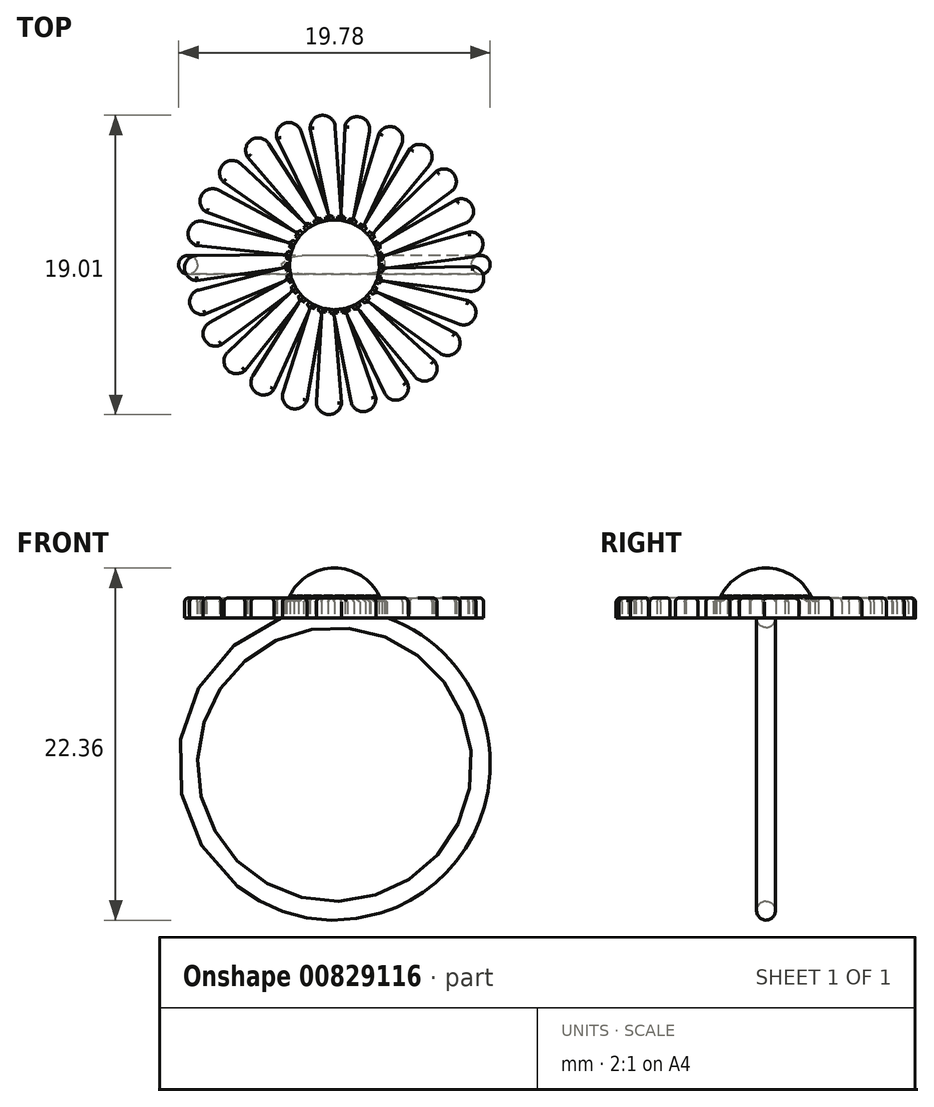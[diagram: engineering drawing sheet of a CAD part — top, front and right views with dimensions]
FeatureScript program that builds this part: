
annotation { "Feature Type Name" : "Feature", "Feature Type Description" : "" }
export const myFeature = defineFeature(function(context is Context, id is Id, definition is map)
    precondition{}
    {
        {
            var Q0;
            Q0=qCreatedBy(makeId("Top.planeOp"),FACE);
            var sketch = newSketch(context, id + "F0", { "sketchPlane" : qUnion([Q0])});
            skCircle(sketch, "E0", {"center": v(0, 0) * mm, "radius": 3.17 * mm});
            skLineSegment(sketch, "E1", {"start": v(-2.86, 1.37) * mm, "end": v(-8.13, 3.33) * mm});
            skLineSegment(sketch, "E2", {"start": v(-2.42, 2.05) * mm, "end": v(-7.36, 4.73) * mm});
            skArc(sketch, "E3", {"start": v(-7.36, 4.73) * mm, "mid": v(-8.44, 4.42) * mm, "end": v(-8.13, 3.33) * mm});
            skLineSegment(sketch, "E4.1.0", {"start": v(-2.86, 1.39) * mm, "end": v(-8.3, 2.75) * mm});
            skArc(sketch, "E4.1.1", {"start": v(-8.3, 2.75) * mm, "mid": v(-9.27, 2.18) * mm, "end": v(-8.7, 1.2) * mm});
            skLineSegment(sketch, "E4.1.2", {"start": v(-3.12, 0.61) * mm, "end": v(-8.7, 1.2) * mm});
            skLineSegment(sketch, "E4.2.0", {"start": v(-3.11, 0.63) * mm, "end": v(-8.73, 0.6) * mm});
            skArc(sketch, "E4.2.1", {"start": v(-8.73, 0.6) * mm, "mid": v(-9.52, -0.2) * mm, "end": v(-8.73, -1) * mm});
            skLineSegment(sketch, "E4.2.2", {"start": v(-3.17, -0.18) * mm, "end": v(-8.73, -1) * mm});
            skLineSegment(sketch, "E4.3.0", {"start": v(-3.17, -0.16) * mm, "end": v(-8.6, -1.6) * mm});
            skArc(sketch, "E4.3.1", {"start": v(-8.6, -1.6) * mm, "mid": v(-9.17, -2.56) * mm, "end": v(-8.21, -3.14) * mm});
            skLineSegment(sketch, "E4.3.2", {"start": v(-3.03, -0.96) * mm, "end": v(-8.21, -3.14) * mm});
            skLineSegment(sketch, "E4.4.0", {"start": v(-3.03, -0.94) * mm, "end": v(-7.94, -3.68) * mm});
            skArc(sketch, "E4.4.1", {"start": v(-7.94, -3.68) * mm, "mid": v(-8.25, -4.76) * mm, "end": v(-7.17, -5.08) * mm});
            skLineSegment(sketch, "E4.4.2", {"start": v(-2.7, -1.69) * mm, "end": v(-7.17, -5.08) * mm});
            skLineSegment(sketch, "E4.5.0", {"start": v(-2.7, -1.67) * mm, "end": v(-6.77, -5.54) * mm});
            skArc(sketch, "E4.5.1", {"start": v(-6.77, -5.54) * mm, "mid": v(-6.8, -6.66) * mm, "end": v(-5.69, -6.7) * mm});
            skLineSegment(sketch, "E4.5.2", {"start": v(-2.19, -2.3) * mm, "end": v(-5.69, -6.7) * mm});
            skLineSegment(sketch, "E4.6.0", {"start": v(-2.2, -2.29) * mm, "end": v(-5.18, -7.05) * mm});
            skArc(sketch, "E4.6.1", {"start": v(-5.18, -7.05) * mm, "mid": v(-4.94, -8.15) * mm, "end": v(-3.84, -7.9) * mm});
            skLineSegment(sketch, "E4.6.2", {"start": v(-1.55, -2.77) * mm, "end": v(-3.84, -7.9) * mm});
            skLineSegment(sketch, "E4.7.0", {"start": v(-1.56, -2.76) * mm, "end": v(-3.27, -8.12) * mm});
            skArc(sketch, "E4.7.1", {"start": v(-3.27, -8.12) * mm, "mid": v(-2.76, -9.12) * mm, "end": v(-1.75, -8.62) * mm});
            skLineSegment(sketch, "E4.7.2", {"start": v(-0.8, -3.07) * mm, "end": v(-1.75, -8.62) * mm});
            skLineSegment(sketch, "E4.8.0", {"start": v(-0.83, -3.07) * mm, "end": v(-1.15, -8.68) * mm});
            skArc(sketch, "E4.8.1", {"start": v(-1.15, -8.68) * mm, "mid": v(-0.4, -9.52) * mm, "end": v(0.45, -8.78) * mm});
            skLineSegment(sketch, "E4.8.2", {"start": v(-0.02, -3.17) * mm, "end": v(0.45, -8.78) * mm});
            skLineSegment(sketch, "E4.9.0", {"start": v(-0.04, -3.17) * mm, "end": v(1.05, -8.69) * mm});
            skArc(sketch, "E4.9.1", {"start": v(1.05, -8.69) * mm, "mid": v(1.98, -9.32) * mm, "end": v(2.62, -8.4) * mm});
            skLineSegment(sketch, "E4.9.2", {"start": v(0.77, -3.08) * mm, "end": v(2.62, -8.4) * mm});
            skLineSegment(sketch, "E4.10.0", {"start": v(0.75, -3.08) * mm, "end": v(3.18, -8.15) * mm});
            skArc(sketch, "E4.10.1", {"start": v(3.18, -8.15) * mm, "mid": v(4.23, -8.53) * mm, "end": v(4.62, -7.48) * mm});
            skLineSegment(sketch, "E4.10.2", {"start": v(1.51, -2.8) * mm, "end": v(4.62, -7.48) * mm});
            skLineSegment(sketch, "E4.11.0", {"start": v(1.5, -2.8) * mm, "end": v(5.1, -7.1) * mm});
            skArc(sketch, "E4.11.1", {"start": v(5.1, -7.1) * mm, "mid": v(6.22, -7.21) * mm, "end": v(6.34, -6.1) * mm});
            skLineSegment(sketch, "E4.11.2", {"start": v(2.16, -2.33) * mm, "end": v(6.34, -6.1) * mm});
            skLineSegment(sketch, "E4.12.0", {"start": v(2.14, -2.34) * mm, "end": v(6.71, -5.62) * mm});
            skArc(sketch, "E4.12.1", {"start": v(6.71, -5.62) * mm, "mid": v(7.82, -5.44) * mm, "end": v(7.65, -4.33) * mm});
            skLineSegment(sketch, "E4.12.2", {"start": v(2.67, -1.72) * mm, "end": v(7.65, -4.33) * mm});
            skLineSegment(sketch, "E4.13.0", {"start": v(2.66, -1.73) * mm, "end": v(7.9, -3.77) * mm});
            skArc(sketch, "E4.13.1", {"start": v(7.9, -3.77) * mm, "mid": v(8.93, -3.32) * mm, "end": v(8.49, -2.29) * mm});
            skLineSegment(sketch, "E4.13.2", {"start": v(3.01, -1) * mm, "end": v(8.49, -2.29) * mm});
            skLineSegment(sketch, "E4.14.0", {"start": v(3, -1.02) * mm, "end": v(8.59, -1.69) * mm});
            skArc(sketch, "E4.14.1", {"start": v(8.59, -1.69) * mm, "mid": v(9.47, -1) * mm, "end": v(8.8, -0.1) * mm});
            skLineSegment(sketch, "E4.14.2", {"start": v(3.17, -0.22) * mm, "end": v(8.8, -0.1) * mm});
            skLineSegment(sketch, "E4.15.0", {"start": v(3.17, -0.24) * mm, "end": v(8.74, 0.5) * mm});
            skArc(sketch, "E4.15.1", {"start": v(8.74, 0.5) * mm, "mid": v(9.42, 1.39) * mm, "end": v(8.54, 2.08) * mm});
            skLineSegment(sketch, "E4.15.2", {"start": v(3.12, 0.58) * mm, "end": v(8.54, 2.08) * mm});
            skLineSegment(sketch, "E4.16.0", {"start": v(3.13, 0.56) * mm, "end": v(8.34, 2.66) * mm});
            skArc(sketch, "E4.16.1", {"start": v(8.34, 2.66) * mm, "mid": v(8.78, 3.69) * mm, "end": v(7.75, 4.14) * mm});
            skLineSegment(sketch, "E4.16.2", {"start": v(2.88, 1.33) * mm, "end": v(7.75, 4.14) * mm});
            skLineSegment(sketch, "E4.17.0", {"start": v(2.89, 1.32) * mm, "end": v(7.41, 4.65) * mm});
            skArc(sketch, "E4.17.1", {"start": v(7.41, 4.65) * mm, "mid": v(7.59, 5.76) * mm, "end": v(6.48, 5.94) * mm});
            skLineSegment(sketch, "E4.17.2", {"start": v(2.46, 2) * mm, "end": v(6.48, 5.94) * mm});
            skLineSegment(sketch, "E4.18.0", {"start": v(2.47, 2) * mm, "end": v(6.03, 6.35) * mm});
            skArc(sketch, "E4.18.1", {"start": v(6.03, 6.35) * mm, "mid": v(5.92, 7.46) * mm, "end": v(4.8, 7.37) * mm});
            skLineSegment(sketch, "E4.18.2", {"start": v(1.88, 2.56) * mm, "end": v(4.8, 7.37) * mm});
            skLineSegment(sketch, "E4.19.0", {"start": v(1.9, 2.55) * mm, "end": v(4.26, 7.64) * mm});
            skArc(sketch, "E4.19.1", {"start": v(4.26, 7.64) * mm, "mid": v(3.88, 8.7) * mm, "end": v(2.82, 8.33) * mm});
            skLineSegment(sketch, "E4.19.2", {"start": v(1.19, 2.95) * mm, "end": v(2.82, 8.33) * mm});
            skLineSegment(sketch, "E4.20.0", {"start": v(1.2, 2.94) * mm, "end": v(2.22, 8.46) * mm});
            skArc(sketch, "E4.20.1", {"start": v(2.22, 8.46) * mm, "mid": v(1.6, 9.4) * mm, "end": v(0.66, 8.77) * mm});
            skLineSegment(sketch, "E4.20.2", {"start": v(0.42, 3.15) * mm, "end": v(0.66, 8.77) * mm});
            skLineSegment(sketch, "E4.21.0", {"start": v(0.44, 3.14) * mm, "end": v(0.05, 8.75) * mm});
            skArc(sketch, "E4.21.1", {"start": v(0.05, 8.75) * mm, "mid": v(-0.8, 9.5) * mm, "end": v(-1.54, 8.65) * mm});
            skLineSegment(sketch, "E4.21.2", {"start": v(-0.38, 3.15) * mm, "end": v(-1.54, 8.65) * mm});
            skLineSegment(sketch, "E4.22.0", {"start": v(-0.36, 3.15) * mm, "end": v(-2.13, 8.49) * mm});
            skArc(sketch, "E4.22.1", {"start": v(-2.13, 8.49) * mm, "mid": v(-3.13, 9) * mm, "end": v(-3.65, 8) * mm});
            skLineSegment(sketch, "E4.22.2", {"start": v(-1.15, 2.96) * mm, "end": v(-3.65, 8) * mm});
            skLineSegment(sketch, "E4.23.0", {"start": v(-1.13, 2.97) * mm, "end": v(-4.17, 7.7) * mm});
            skArc(sketch, "E4.23.1", {"start": v(-4.17, 7.7) * mm, "mid": v(-5.27, 7.93) * mm, "end": v(-5.52, 6.84) * mm});
            skLineSegment(sketch, "E4.23.2", {"start": v(-1.85, 2.58) * mm, "end": v(-5.52, 6.84) * mm});
            skLineSegment(sketch, "E4.24.0", {"start": v(-1.83, 2.6) * mm, "end": v(-5.95, 6.41) * mm});
            skArc(sketch, "E4.24.1", {"start": v(-5.95, 6.41) * mm, "mid": v(-7.08, 6.38) * mm, "end": v(-7.05, 5.25) * mm});
            skLineSegment(sketch, "E4.24.2", {"start": v(-2.43, 2.04) * mm, "end": v(-7.05, 5.25) * mm});
            skLineSegment(sketch, "E5", {"start": v(0, 0) * mm, "end": v(0, 3.17) * mm});
            skLineSegment(sketch, "E6", {"start": v(0, 0) * mm, "end": v(0, -3.17) * mm});
            skLineSegment(sketch, "E7", {"start": v(0, 3.17) * mm, "end": v(0, -3.17) * mm, "construction": true});
            skSolve(sketch);
        }
        {
            var Q0;
            Q0 = qSketchRegion(id + "F0", true);
            var Q1;
            {var subQ18=sQuery(id+"F0.wireOp",EDGE,"E5");Q1=makeQuery(id+"F0.imprint","IMPRINT",FACE,{"disambiguationData":[TD([[makeQuery(id+"F0.imprint","IMPRINT",EDGE,{"derivedFrom":subQ18}),1.0]])]});}
            var Q2;
            {var subQ4=sQuery(id+"F0.wireOp",EDGE,"E5");Q2=makeQuery(id+"F0.imprint","IMPRINT",FACE,{"disambiguationData":[TD([[makeQuery(id+"F0.imprint","IMPRINT",EDGE,{"derivedFrom":subQ4}),-1.0]])]});}
            extrude(context, id + "F1", {"entities" : qUnion([Q0, Q1, Q2]), "depth" : 1.27 * mm, "offsetDistance" : 25.4 * mm});
        }
        {
            var Q0;
            {var subQ18=sQuery(id+"F0.wireOp",EDGE,"E5");Q0=makeQuery(id+"F0.imprint","IMPRINT",FACE,{"disambiguationData":[TD([[makeQuery(id+"F0.imprint","IMPRINT",EDGE,{"derivedFrom":subQ18}),1.0]])]});}
            var Q1;
            Q1=sQuery(id+"F0.wireOp",EDGE,"E6");
            revolve(context, id + "F2", {"operationType" : NewBodyOperationType.ADD, "surfaceOperationType" : NewSurfaceOperationType.NEW, "entities" : qUnion([Q0]), "axis" : qUnion([Q1]), "revolveType" : RevolveType.ONE_DIRECTION, "oppositeDirection" : true, "angle" : 180 * degree});
        }
        {
            var Q0;
            Q0=makeQuery(id+"F1.opExtrude","CAP_EDGE",EDGE,{"disambiguationData":[OSD([sQuery(id+"F0.wireOp",EDGE,"E3")])],"isStart":false});
            var Q1;
            Q1=makeQuery(id+"F1.opExtrude","CAP_EDGE",EDGE,{"disambiguationData":[OSD([sQuery(id+"F0.wireOp",EDGE,"E1")])],"isStart":false});
            var Q2;
            Q2=makeQuery(id+"F1.opExtrude","CAP_EDGE",EDGE,{"disambiguationData":[OSD([sQuery(id+"F0.wireOp",EDGE,"E2")])],"isStart":false});
            var Q3;
            Q3=makeQuery(id+"F1.opExtrude","CAP_EDGE",EDGE,{"disambiguationData":[OSD([sQuery(id+"F0.wireOp",EDGE,"E4.24.1")])],"isStart":false});
            var Q4;
            Q4=makeQuery(id+"F1.opExtrude","CAP_EDGE",EDGE,{"disambiguationData":[OSD([sQuery(id+"F0.wireOp",EDGE,"E4.24.2")])],"isStart":false});
            var Q5;
            Q5=makeQuery(id+"F1.opExtrude","CAP_EDGE",EDGE,{"disambiguationData":[OSD([sQuery(id+"F0.wireOp",EDGE,"E4.24.0")])],"isStart":false});
            var Q6;
            Q6=makeQuery(id+"F1.opExtrude","CAP_EDGE",EDGE,{"disambiguationData":[OSD([sQuery(id+"F0.wireOp",EDGE,"E4.23.2")])],"isStart":false});
            var Q7;
            Q7=makeQuery(id+"F1.opExtrude","CAP_EDGE",EDGE,{"disambiguationData":[OSD([sQuery(id+"F0.wireOp",EDGE,"E4.23.1")])],"isStart":false});
            var Q8;
            Q8=makeQuery(id+"F1.opExtrude","CAP_EDGE",EDGE,{"disambiguationData":[OSD([sQuery(id+"F0.wireOp",EDGE,"E4.23.0")])],"isStart":false});
            var Q9;
            Q9=makeQuery(id+"F1.opExtrude","CAP_EDGE",EDGE,{"disambiguationData":[OSD([sQuery(id+"F0.wireOp",EDGE,"E4.22.2")])],"isStart":false});
            var Q10;
            Q10=makeQuery(id+"F1.opExtrude","CAP_EDGE",EDGE,{"disambiguationData":[OSD([sQuery(id+"F0.wireOp",EDGE,"E4.22.1")])],"isStart":false});
            var Q11;
            Q11=makeQuery(id+"F1.opExtrude","CAP_EDGE",EDGE,{"disambiguationData":[OSD([sQuery(id+"F0.wireOp",EDGE,"E4.22.0")])],"isStart":false});
            var Q12;
            Q12=makeQuery(id+"F1.opExtrude","CAP_EDGE",EDGE,{"disambiguationData":[OSD([sQuery(id+"F0.wireOp",EDGE,"E4.21.1")])],"isStart":false});
            var Q13;
            Q13=makeQuery(id+"F1.opExtrude","CAP_EDGE",EDGE,{"disambiguationData":[OSD([sQuery(id+"F0.wireOp",EDGE,"E4.21.2")])],"isStart":false});
            var Q14;
            Q14=makeQuery(id+"F1.opExtrude","CAP_EDGE",EDGE,{"disambiguationData":[OSD([sQuery(id+"F0.wireOp",EDGE,"E4.21.0")])],"isStart":false});
            var Q15;
            Q15=makeQuery(id+"F1.opExtrude","CAP_EDGE",EDGE,{"disambiguationData":[OSD([sQuery(id+"F0.wireOp",EDGE,"E4.20.2")])],"isStart":false});
            var Q16;
            Q16=makeQuery(id+"F1.opExtrude","CAP_EDGE",EDGE,{"disambiguationData":[OSD([sQuery(id+"F0.wireOp",EDGE,"E4.20.1")])],"isStart":false});
            var Q17;
            Q17=makeQuery(id+"F1.opExtrude","CAP_EDGE",EDGE,{"disambiguationData":[OSD([sQuery(id+"F0.wireOp",EDGE,"E4.19.2")])],"isStart":false});
            var Q18;
            Q18=makeQuery(id+"F1.opExtrude","CAP_EDGE",EDGE,{"disambiguationData":[OSD([sQuery(id+"F0.wireOp",EDGE,"E4.19.1")])],"isStart":false});
            var Q19;
            Q19=makeQuery(id+"F1.opExtrude","CAP_EDGE",EDGE,{"disambiguationData":[OSD([sQuery(id+"F0.wireOp",EDGE,"E4.19.0")])],"isStart":false});
            var Q20;
            Q20=makeQuery(id+"F1.opExtrude","CAP_EDGE",EDGE,{"disambiguationData":[OSD([sQuery(id+"F0.wireOp",EDGE,"E4.1.1")])],"isStart":false});
            var Q21;
            Q21=makeQuery(id+"F1.opExtrude","CAP_EDGE",EDGE,{"disambiguationData":[OSD([sQuery(id+"F0.wireOp",EDGE,"E4.1.2")])],"isStart":false});
            var Q22;
            Q22=makeQuery(id+"F1.opExtrude","CAP_EDGE",EDGE,{"disambiguationData":[OSD([sQuery(id+"F0.wireOp",EDGE,"E4.1.0")])],"isStart":false});
            var Q23;
            Q23=makeQuery(id+"F1.opExtrude","CAP_EDGE",EDGE,{"disambiguationData":[OSD([sQuery(id+"F0.wireOp",EDGE,"E4.2.1")])],"isStart":false});
            var Q24;
            Q24=makeQuery(id+"F1.opExtrude","CAP_EDGE",EDGE,{"disambiguationData":[OSD([sQuery(id+"F0.wireOp",EDGE,"E4.2.0")])],"isStart":false});
            var Q25;
            Q25=makeQuery(id+"F1.opExtrude","CAP_EDGE",EDGE,{"disambiguationData":[OSD([sQuery(id+"F0.wireOp",EDGE,"E4.18.2")])],"isStart":false});
            var Q26;
            Q26=makeQuery(id+"F1.opExtrude","CAP_EDGE",EDGE,{"disambiguationData":[OSD([sQuery(id+"F0.wireOp",EDGE,"E4.18.0")])],"isStart":false});
            var Q27;
            Q27=makeQuery(id+"F1.opExtrude","CAP_EDGE",EDGE,{"disambiguationData":[OSD([sQuery(id+"F0.wireOp",EDGE,"E4.18.1")])],"isStart":false});
            var Q28;
            Q28=makeQuery(id+"F1.opExtrude","CAP_EDGE",EDGE,{"disambiguationData":[OSD([sQuery(id+"F0.wireOp",EDGE,"E4.17.1")])],"isStart":false});
            var Q29;
            Q29=makeQuery(id+"F1.opExtrude","CAP_EDGE",EDGE,{"disambiguationData":[OSD([sQuery(id+"F0.wireOp",EDGE,"E4.17.2")])],"isStart":false});
            var Q30;
            Q30=makeQuery(id+"F1.opExtrude","CAP_EDGE",EDGE,{"disambiguationData":[OSD([sQuery(id+"F0.wireOp",EDGE,"E4.17.0")])],"isStart":false});
            var Q31;
            Q31=makeQuery(id+"F1.opExtrude","CAP_EDGE",EDGE,{"disambiguationData":[OSD([sQuery(id+"F0.wireOp",EDGE,"E4.16.2")])],"isStart":false});
            var Q32;
            Q32=makeQuery(id+"F1.opExtrude","CAP_EDGE",EDGE,{"disambiguationData":[OSD([sQuery(id+"F0.wireOp",EDGE,"E4.16.1")])],"isStart":false});
            var Q33;
            Q33=makeQuery(id+"F1.opExtrude","CAP_EDGE",EDGE,{"disambiguationData":[OSD([sQuery(id+"F0.wireOp",EDGE,"E4.16.0")])],"isStart":false});
            var Q34;
            Q34=makeQuery(id+"F1.opExtrude","CAP_EDGE",EDGE,{"disambiguationData":[OSD([sQuery(id+"F0.wireOp",EDGE,"E4.15.2")])],"isStart":false});
            var Q35;
            Q35=makeQuery(id+"F1.opExtrude","CAP_EDGE",EDGE,{"disambiguationData":[OSD([sQuery(id+"F0.wireOp",EDGE,"E4.15.1")])],"isStart":false});
            var Q36;
            Q36=makeQuery(id+"F1.opExtrude","CAP_EDGE",EDGE,{"disambiguationData":[OSD([sQuery(id+"F0.wireOp",EDGE,"E4.15.0")])],"isStart":false});
            var Q37;
            Q37=makeQuery(id+"F1.opExtrude","CAP_EDGE",EDGE,{"disambiguationData":[OSD([sQuery(id+"F0.wireOp",EDGE,"E4.14.2")])],"isStart":false});
            var Q38;
            Q38=makeQuery(id+"F1.opExtrude","CAP_EDGE",EDGE,{"disambiguationData":[OSD([sQuery(id+"F0.wireOp",EDGE,"E4.14.1")])],"isStart":false});
            var Q39;
            Q39=makeQuery(id+"F1.opExtrude","CAP_EDGE",EDGE,{"disambiguationData":[OSD([sQuery(id+"F0.wireOp",EDGE,"E4.14.0")])],"isStart":false});
            var Q40;
            Q40=makeQuery(id+"F1.opExtrude","CAP_EDGE",EDGE,{"disambiguationData":[OSD([sQuery(id+"F0.wireOp",EDGE,"E4.13.2")])],"isStart":false});
            var Q41;
            Q41=makeQuery(id+"F1.opExtrude","CAP_EDGE",EDGE,{"disambiguationData":[OSD([sQuery(id+"F0.wireOp",EDGE,"E4.13.1")])],"isStart":false});
            var Q42;
            Q42=makeQuery(id+"F1.opExtrude","CAP_EDGE",EDGE,{"disambiguationData":[OSD([sQuery(id+"F0.wireOp",EDGE,"E4.13.0")])],"isStart":false});
            var Q43;
            Q43=makeQuery(id+"F1.opExtrude","CAP_EDGE",EDGE,{"disambiguationData":[OSD([sQuery(id+"F0.wireOp",EDGE,"E4.12.2")])],"isStart":false});
            var Q44;
            Q44=makeQuery(id+"F1.opExtrude","CAP_EDGE",EDGE,{"disambiguationData":[OSD([sQuery(id+"F0.wireOp",EDGE,"E4.12.1")])],"isStart":false});
            var Q45;
            Q45=makeQuery(id+"F1.opExtrude","CAP_EDGE",EDGE,{"disambiguationData":[OSD([sQuery(id+"F0.wireOp",EDGE,"E4.12.0")])],"isStart":false});
            var Q46;
            Q46=makeQuery(id+"F1.opExtrude","CAP_EDGE",EDGE,{"disambiguationData":[OSD([sQuery(id+"F0.wireOp",EDGE,"E4.11.2")])],"isStart":false});
            var Q47;
            Q47=makeQuery(id+"F1.opExtrude","CAP_EDGE",EDGE,{"disambiguationData":[OSD([sQuery(id+"F0.wireOp",EDGE,"E4.11.1")])],"isStart":false});
            var Q48;
            Q48=makeQuery(id+"F1.opExtrude","CAP_EDGE",EDGE,{"disambiguationData":[OSD([sQuery(id+"F0.wireOp",EDGE,"E4.11.0")])],"isStart":false});
            var Q49;
            Q49=makeQuery(id+"F1.opExtrude","CAP_EDGE",EDGE,{"disambiguationData":[OSD([sQuery(id+"F0.wireOp",EDGE,"E4.10.2")])],"isStart":false});
            var Q50;
            Q50=makeQuery(id+"F1.opExtrude","CAP_EDGE",EDGE,{"disambiguationData":[OSD([sQuery(id+"F0.wireOp",EDGE,"E4.10.1")])],"isStart":false});
            var Q51;
            Q51=makeQuery(id+"F1.opExtrude","CAP_EDGE",EDGE,{"disambiguationData":[OSD([sQuery(id+"F0.wireOp",EDGE,"E4.10.0")])],"isStart":false});
            var Q52;
            Q52=makeQuery(id+"F1.opExtrude","CAP_EDGE",EDGE,{"disambiguationData":[OSD([sQuery(id+"F0.wireOp",EDGE,"E4.2.2")])],"isStart":false});
            var Q53;
            Q53=makeQuery(id+"F1.opExtrude","CAP_EDGE",EDGE,{"disambiguationData":[OSD([sQuery(id+"F0.wireOp",EDGE,"E4.3.0")])],"isStart":false});
            var Q54;
            Q54=makeQuery(id+"F1.opExtrude","CAP_EDGE",EDGE,{"disambiguationData":[OSD([sQuery(id+"F0.wireOp",EDGE,"E4.3.1")])],"isStart":false});
            var Q55;
            Q55=makeQuery(id+"F1.opExtrude","CAP_EDGE",EDGE,{"disambiguationData":[OSD([sQuery(id+"F0.wireOp",EDGE,"E4.3.2")])],"isStart":false});
            var Q56;
            Q56=makeQuery(id+"F1.opExtrude","CAP_EDGE",EDGE,{"disambiguationData":[OSD([sQuery(id+"F0.wireOp",EDGE,"E4.4.0")])],"isStart":false});
            var Q57;
            Q57=makeQuery(id+"F1.opExtrude","CAP_EDGE",EDGE,{"disambiguationData":[OSD([sQuery(id+"F0.wireOp",EDGE,"E4.4.1")])],"isStart":false});
            var Q58;
            Q58=makeQuery(id+"F1.opExtrude","CAP_EDGE",EDGE,{"disambiguationData":[OSD([sQuery(id+"F0.wireOp",EDGE,"E4.4.2")])],"isStart":false});
            var Q59;
            Q59=makeQuery(id+"F1.opExtrude","CAP_EDGE",EDGE,{"disambiguationData":[OSD([sQuery(id+"F0.wireOp",EDGE,"E4.5.0")])],"isStart":false});
            var Q60;
            Q60=makeQuery(id+"F1.opExtrude","CAP_EDGE",EDGE,{"disambiguationData":[OSD([sQuery(id+"F0.wireOp",EDGE,"E4.5.1")])],"isStart":false});
            var Q61;
            Q61=makeQuery(id+"F1.opExtrude","CAP_EDGE",EDGE,{"disambiguationData":[OSD([sQuery(id+"F0.wireOp",EDGE,"E4.5.2")])],"isStart":false});
            var Q62;
            Q62=makeQuery(id+"F1.opExtrude","CAP_EDGE",EDGE,{"disambiguationData":[OSD([sQuery(id+"F0.wireOp",EDGE,"E4.6.0")])],"isStart":false});
            var Q63;
            Q63=makeQuery(id+"F1.opExtrude","CAP_EDGE",EDGE,{"disambiguationData":[OSD([sQuery(id+"F0.wireOp",EDGE,"E4.6.1")])],"isStart":false});
            var Q64;
            Q64=makeQuery(id+"F1.opExtrude","CAP_EDGE",EDGE,{"disambiguationData":[OSD([sQuery(id+"F0.wireOp",EDGE,"E4.6.2")])],"isStart":false});
            var Q65;
            Q65=makeQuery(id+"F1.opExtrude","CAP_EDGE",EDGE,{"disambiguationData":[OSD([sQuery(id+"F0.wireOp",EDGE,"E4.7.0")])],"isStart":false});
            var Q66;
            Q66=makeQuery(id+"F1.opExtrude","CAP_EDGE",EDGE,{"disambiguationData":[OSD([sQuery(id+"F0.wireOp",EDGE,"E4.7.1")])],"isStart":false});
            var Q67;
            Q67=makeQuery(id+"F1.opExtrude","CAP_EDGE",EDGE,{"disambiguationData":[OSD([sQuery(id+"F0.wireOp",EDGE,"E4.7.2")])],"isStart":false});
            var Q68;
            Q68=makeQuery(id+"F1.opExtrude","CAP_EDGE",EDGE,{"disambiguationData":[OSD([sQuery(id+"F0.wireOp",EDGE,"E4.8.0")])],"isStart":false});
            var Q69;
            Q69=makeQuery(id+"F1.opExtrude","CAP_EDGE",EDGE,{"disambiguationData":[OSD([sQuery(id+"F0.wireOp",EDGE,"E4.8.1")])],"isStart":false});
            var Q70;
            Q70=makeQuery(id+"F1.opExtrude","CAP_EDGE",EDGE,{"disambiguationData":[OSD([sQuery(id+"F0.wireOp",EDGE,"E4.8.2")])],"isStart":false});
            var Q71;
            Q71=makeQuery(id+"F1.opExtrude","CAP_EDGE",EDGE,{"disambiguationData":[OSD([sQuery(id+"F0.wireOp",EDGE,"E4.9.0")])],"isStart":false});
            var Q72;
            Q72=makeQuery(id+"F1.opExtrude","CAP_EDGE",EDGE,{"disambiguationData":[OSD([sQuery(id+"F0.wireOp",EDGE,"E4.9.1")])],"isStart":false});
            var Q73;
            Q73=makeQuery(id+"F1.opExtrude","CAP_EDGE",EDGE,{"disambiguationData":[OSD([sQuery(id+"F0.wireOp",EDGE,"E4.9.2")])],"isStart":false});
            var Q74;
            Q74=makeQuery(id+"F1.opExtrude","CAP_EDGE",EDGE,{"disambiguationData":[OSD([sQuery(id+"F0.wireOp",EDGE,"E4.20.0")])],"isStart":false});
            fillet(context, id + "F3", {"entities" : qUnion([Q0, Q1, Q2, Q3, Q4, Q5, Q6, Q7, Q8, Q9, Q10, Q11, Q12, Q13, Q14, Q15, Q16, Q17, Q18, Q19, Q20, Q21, Q22, Q23, Q24, Q25, Q26, Q27, Q28, Q29, Q30, Q31, Q32, Q33, Q34, Q35, Q36, Q37, Q38, Q39, Q40, Q41, Q42, Q43, Q44, Q45, Q46, Q47, Q48, Q49, Q50, Q51, Q52, Q53, Q54, Q55, Q56, Q57, Q58, Q59, Q60, Q61, Q62, Q63, Q64, Q65, Q66, Q67, Q68, Q69, Q70, Q71, Q72, Q73, Q74]), "radius" : 0.25 * mm, "tangentPropagation" : true, "allowEdgeOverflow" : false});
        }
        {
            var Q0;
            Q0=qCreatedBy(makeId("Right.planeOp"),FACE);
            var sketch = newSketch(context, id + "F4", { "sketchPlane" : qUnion([Q0])});
            skCircle(sketch, "E8", {"center": v(0, 0) * mm, "radius": 0.6 * mm});
            skLineSegment(sketch, "E9", {"start": v(0, 0) * mm, "end": v(0, -18.6) * mm, "construction": true});
            skCircle(sketch, "E10", {"center": v(0, -18.6) * mm, "radius": 0.6 * mm});
            skPoint(sketch, "E11", {"position": v(0, -9.3) * mm});
            skLineSegment(sketch, "E12", {"start": v(-8.96, -9.3) * mm, "end": v(8.87, -9.3) * mm, "construction": true});
            skSolve(sketch);
        }
        {
            var Q0;
            Q0=makeQuery(id+"F4.imprint","IMPRINT",FACE,{"disambiguationData":[TD([[makeQuery(id+"F4.imprint","IMPRINT",EDGE,{"derivedFrom":sQuery(id+"F4.wireOp",EDGE,"E10")}),1.0]])]});
            var Q1;
            Q1=sQuery(id+"F4.wireOp",EDGE,"E12");
            revolve(context, id + "F5", {"operationType" : NewBodyOperationType.ADD, "surfaceOperationType" : NewSurfaceOperationType.NEW, "entities" : qUnion([Q0]), "axis" : qUnion([Q1]), "revolveType" : RevolveType.FULL});
        }
        {
            var Q0;
            Q0=makeQuery(id+"F2.boolean.opBoolean","INTERSECT",EDGE,{"derivedFrom":[makeQuery(id+"F1.opExtrude","CAP_FACE",FACE,{"disambiguationData":[OSD([sQuery(id+"F0.wireOp",EDGE,"E1"),sQuery(id+"F0.wireOp",EDGE,"E2"),sQuery(id+"F0.wireOp",EDGE,"E3"),sQuery(id+"F0.wireOp",EDGE,"E4.1.0"),sQuery(id+"F0.wireOp",EDGE,"E4.1.1"),sQuery(id+"F0.wireOp",EDGE,"E4.1.2"),sQuery(id+"F0.wireOp",EDGE,"E4.2.0"),sQuery(id+"F0.wireOp",EDGE,"E4.2.1"),sQuery(id+"F0.wireOp",EDGE,"E4.2.2"),sQuery(id+"F0.wireOp",EDGE,"E4.3.0"),sQuery(id+"F0.wireOp",EDGE,"E4.3.1"),sQuery(id+"F0.wireOp",EDGE,"E4.3.2"),sQuery(id+"F0.wireOp",EDGE,"E4.4.0"),sQuery(id+"F0.wireOp",EDGE,"E4.4.1"),sQuery(id+"F0.wireOp",EDGE,"E4.4.2"),sQuery(id+"F0.wireOp",EDGE,"E4.5.0"),sQuery(id+"F0.wireOp",EDGE,"E4.5.1"),sQuery(id+"F0.wireOp",EDGE,"E4.5.2"),sQuery(id+"F0.wireOp",EDGE,"E4.6.0"),sQuery(id+"F0.wireOp",EDGE,"E4.6.1"),sQuery(id+"F0.wireOp",EDGE,"E4.6.2"),sQuery(id+"F0.wireOp",EDGE,"E4.7.0"),sQuery(id+"F0.wireOp",EDGE,"E4.7.1"),sQuery(id+"F0.wireOp",EDGE,"E4.7.2"),sQuery(id+"F0.wireOp",EDGE,"E4.8.0"),sQuery(id+"F0.wireOp",EDGE,"E4.8.1"),sQuery(id+"F0.wireOp",EDGE,"E4.8.2"),sQuery(id+"F0.wireOp",EDGE,"E4.9.0"),sQuery(id+"F0.wireOp",EDGE,"E4.9.1"),sQuery(id+"F0.wireOp",EDGE,"E4.9.2"),sQuery(id+"F0.wireOp",EDGE,"E4.10.0"),sQuery(id+"F0.wireOp",EDGE,"E4.10.1"),sQuery(id+"F0.wireOp",EDGE,"E4.10.2"),sQuery(id+"F0.wireOp",EDGE,"E4.11.0"),sQuery(id+"F0.wireOp",EDGE,"E4.11.1"),sQuery(id+"F0.wireOp",EDGE,"E4.11.2"),sQuery(id+"F0.wireOp",EDGE,"E4.12.0"),sQuery(id+"F0.wireOp",EDGE,"E4.12.1"),sQuery(id+"F0.wireOp",EDGE,"E4.12.2"),sQuery(id+"F0.wireOp",EDGE,"E4.13.0"),sQuery(id+"F0.wireOp",EDGE,"E4.13.1"),sQuery(id+"F0.wireOp",EDGE,"E4.13.2"),sQuery(id+"F0.wireOp",EDGE,"E4.14.0"),sQuery(id+"F0.wireOp",EDGE,"E4.14.1"),sQuery(id+"F0.wireOp",EDGE,"E4.14.2"),sQuery(id+"F0.wireOp",EDGE,"E4.15.0"),sQuery(id+"F0.wireOp",EDGE,"E4.15.1"),sQuery(id+"F0.wireOp",EDGE,"E4.15.2"),sQuery(id+"F0.wireOp",EDGE,"E4.16.0"),sQuery(id+"F0.wireOp",EDGE,"E4.16.1"),sQuery(id+"F0.wireOp",EDGE,"E4.16.2"),sQuery(id+"F0.wireOp",EDGE,"E4.17.0"),sQuery(id+"F0.wireOp",EDGE,"E4.17.1"),sQuery(id+"F0.wireOp",EDGE,"E4.17.2"),sQuery(id+"F0.wireOp",EDGE,"E4.18.0"),sQuery(id+"F0.wireOp",EDGE,"E4.18.1"),sQuery(id+"F0.wireOp",EDGE,"E4.18.2"),sQuery(id+"F0.wireOp",EDGE,"E4.19.0"),sQuery(id+"F0.wireOp",EDGE,"E4.19.1"),sQuery(id+"F0.wireOp",EDGE,"E4.19.2"),sQuery(id+"F0.wireOp",EDGE,"E4.20.0"),sQuery(id+"F0.wireOp",EDGE,"E4.20.1"),sQuery(id+"F0.wireOp",EDGE,"E4.20.2"),sQuery(id+"F0.wireOp",EDGE,"E4.21.0"),sQuery(id+"F0.wireOp",EDGE,"E4.21.1"),sQuery(id+"F0.wireOp",EDGE,"E4.21.2"),sQuery(id+"F0.wireOp",EDGE,"E4.22.0"),sQuery(id+"F0.wireOp",EDGE,"E4.22.1"),sQuery(id+"F0.wireOp",EDGE,"E4.22.2"),sQuery(id+"F0.wireOp",EDGE,"E4.23.0"),sQuery(id+"F0.wireOp",EDGE,"E4.23.1"),sQuery(id+"F0.wireOp",EDGE,"E4.23.2"),sQuery(id+"F0.wireOp",EDGE,"E4.24.0"),sQuery(id+"F0.wireOp",EDGE,"E4.24.1"),sQuery(id+"F0.wireOp",EDGE,"E4.24.2")])],"isStart":false}),makeQuery(id+"F2.opRevolve","SWEPT_FACE",FACE,{"disambiguationData":[OSD([sQuery(id+"F0.wireOp",EDGE,"E0")])]})]});
            var Q1;
            Q1=makeQuery(id+"F3.opFillet","BLEND_EDGE",EDGE,{"blendedFrom":[makeQuery(id+"F1.opExtrude","CAP_EDGE",EDGE,{"disambiguationData":[OSD([sQuery(id+"F0.wireOp",EDGE,"E4.24.0")])],"isStart":false}),makeQuery(id+"F2.opRevolve","SWEPT_FACE",FACE,{"disambiguationData":[OSD([sQuery(id+"F0.wireOp",EDGE,"E0")])]})],"blendedInto":[makeQuery(id+"F2.opRevolve","SWEPT_FACE",FACE,{"disambiguationData":[OSD([sQuery(id+"F0.wireOp",EDGE,"E0")])]})]});
            var Q2;
            Q2=makeQuery(id+"F3.opFillet","BLEND_EDGE",EDGE,{"blendedFrom":[makeQuery(id+"F1.opExtrude","CAP_EDGE",EDGE,{"disambiguationData":[OSD([sQuery(id+"F0.wireOp",EDGE,"E4.24.2")])],"isStart":false}),makeQuery(id+"F2.opRevolve","SWEPT_FACE",FACE,{"disambiguationData":[OSD([sQuery(id+"F0.wireOp",EDGE,"E0")])]})],"blendedInto":[makeQuery(id+"F2.opRevolve","SWEPT_FACE",FACE,{"disambiguationData":[OSD([sQuery(id+"F0.wireOp",EDGE,"E0")])]})]});
            var Q3;
            Q3=makeQuery(id+"F3.opFillet","BLEND_EDGE",EDGE,{"blendedFrom":[makeQuery(id+"F1.opExtrude","CAP_EDGE",EDGE,{"disambiguationData":[OSD([sQuery(id+"F0.wireOp",EDGE,"E2")])],"isStart":false}),makeQuery(id+"F2.opRevolve","SWEPT_FACE",FACE,{"disambiguationData":[OSD([sQuery(id+"F0.wireOp",EDGE,"E0")])]})],"blendedInto":[makeQuery(id+"F2.opRevolve","SWEPT_FACE",FACE,{"disambiguationData":[OSD([sQuery(id+"F0.wireOp",EDGE,"E0")])]})]});
            var Q4;
            Q4=makeQuery(id+"F3.opFillet","BLEND_EDGE",EDGE,{"blendedFrom":[makeQuery(id+"F1.opExtrude","CAP_EDGE",EDGE,{"disambiguationData":[OSD([sQuery(id+"F0.wireOp",EDGE,"E1")])],"isStart":false}),makeQuery(id+"F2.opRevolve","SWEPT_FACE",FACE,{"disambiguationData":[OSD([sQuery(id+"F0.wireOp",EDGE,"E0")])]})],"blendedInto":[makeQuery(id+"F2.opRevolve","SWEPT_FACE",FACE,{"disambiguationData":[OSD([sQuery(id+"F0.wireOp",EDGE,"E0")])]})]});
            var Q5;
            Q5=makeQuery(id+"F3.opFillet","BLEND_EDGE",EDGE,{"blendedFrom":[makeQuery(id+"F1.opExtrude","CAP_EDGE",EDGE,{"disambiguationData":[OSD([sQuery(id+"F0.wireOp",EDGE,"E4.1.0")])],"isStart":false}),makeQuery(id+"F2.opRevolve","SWEPT_FACE",FACE,{"disambiguationData":[OSD([sQuery(id+"F0.wireOp",EDGE,"E0")])]})],"blendedInto":[makeQuery(id+"F2.opRevolve","SWEPT_FACE",FACE,{"disambiguationData":[OSD([sQuery(id+"F0.wireOp",EDGE,"E0")])]})]});
            var Q6;
            Q6=makeQuery(id+"F3.opFillet","BLEND_EDGE",EDGE,{"blendedFrom":[makeQuery(id+"F1.opExtrude","CAP_EDGE",EDGE,{"disambiguationData":[OSD([sQuery(id+"F0.wireOp",EDGE,"E4.1.2")])],"isStart":false}),makeQuery(id+"F2.opRevolve","SWEPT_FACE",FACE,{"disambiguationData":[OSD([sQuery(id+"F0.wireOp",EDGE,"E0")])]})],"blendedInto":[makeQuery(id+"F2.opRevolve","SWEPT_FACE",FACE,{"disambiguationData":[OSD([sQuery(id+"F0.wireOp",EDGE,"E0")])]})]});
            var Q7;
            Q7=makeQuery(id+"F3.opFillet","BLEND_EDGE",EDGE,{"blendedFrom":[makeQuery(id+"F1.opExtrude","CAP_EDGE",EDGE,{"disambiguationData":[OSD([sQuery(id+"F0.wireOp",EDGE,"E4.23.2")])],"isStart":false}),makeQuery(id+"F2.opRevolve","SWEPT_FACE",FACE,{"disambiguationData":[OSD([sQuery(id+"F0.wireOp",EDGE,"E0")])]})],"blendedInto":[makeQuery(id+"F2.opRevolve","SWEPT_FACE",FACE,{"disambiguationData":[OSD([sQuery(id+"F0.wireOp",EDGE,"E0")])]})]});
            var Q8;
            Q8=makeQuery(id+"F3.opFillet","BLEND_EDGE",EDGE,{"blendedFrom":[makeQuery(id+"F1.opExtrude","CAP_EDGE",EDGE,{"disambiguationData":[OSD([sQuery(id+"F0.wireOp",EDGE,"E4.23.0")])],"isStart":false}),makeQuery(id+"F2.opRevolve","SWEPT_FACE",FACE,{"disambiguationData":[OSD([sQuery(id+"F0.wireOp",EDGE,"E0")])]})],"blendedInto":[makeQuery(id+"F2.opRevolve","SWEPT_FACE",FACE,{"disambiguationData":[OSD([sQuery(id+"F0.wireOp",EDGE,"E0")])]})]});
            var Q9;
            Q9=makeQuery(id+"F3.opFillet","BLEND_EDGE",EDGE,{"blendedFrom":[makeQuery(id+"F1.opExtrude","CAP_EDGE",EDGE,{"disambiguationData":[OSD([sQuery(id+"F0.wireOp",EDGE,"E4.22.2")])],"isStart":false}),makeQuery(id+"F2.opRevolve","SWEPT_FACE",FACE,{"disambiguationData":[OSD([sQuery(id+"F0.wireOp",EDGE,"E0")])]})],"blendedInto":[makeQuery(id+"F2.opRevolve","SWEPT_FACE",FACE,{"disambiguationData":[OSD([sQuery(id+"F0.wireOp",EDGE,"E0")])]})]});
            var Q10;
            Q10=makeQuery(id+"F3.opFillet","BLEND_EDGE",EDGE,{"blendedFrom":[makeQuery(id+"F1.opExtrude","CAP_EDGE",EDGE,{"disambiguationData":[OSD([sQuery(id+"F0.wireOp",EDGE,"E4.22.0")])],"isStart":false}),makeQuery(id+"F2.opRevolve","SWEPT_FACE",FACE,{"disambiguationData":[OSD([sQuery(id+"F0.wireOp",EDGE,"E0")])]})],"blendedInto":[makeQuery(id+"F2.opRevolve","SWEPT_FACE",FACE,{"disambiguationData":[OSD([sQuery(id+"F0.wireOp",EDGE,"E0")])]})]});
            var Q11;
            Q11=makeQuery(id+"F3.opFillet","BLEND_EDGE",EDGE,{"blendedFrom":[makeQuery(id+"F1.opExtrude","CAP_EDGE",EDGE,{"disambiguationData":[OSD([sQuery(id+"F0.wireOp",EDGE,"E4.21.0")])],"isStart":false}),makeQuery(id+"F2.opRevolve","SWEPT_FACE",FACE,{"disambiguationData":[OSD([sQuery(id+"F0.wireOp",EDGE,"E0")])]})],"blendedInto":[makeQuery(id+"F2.opRevolve","SWEPT_FACE",FACE,{"disambiguationData":[OSD([sQuery(id+"F0.wireOp",EDGE,"E0")])]})]});
            var Q12;
            Q12=makeQuery(id+"F3.opFillet","BLEND_EDGE",EDGE,{"blendedFrom":[makeQuery(id+"F1.opExtrude","CAP_EDGE",EDGE,{"disambiguationData":[OSD([sQuery(id+"F0.wireOp",EDGE,"E4.21.2")])],"isStart":false}),makeQuery(id+"F2.opRevolve","SWEPT_FACE",FACE,{"disambiguationData":[OSD([sQuery(id+"F0.wireOp",EDGE,"E0")])]})],"blendedInto":[makeQuery(id+"F2.opRevolve","SWEPT_FACE",FACE,{"disambiguationData":[OSD([sQuery(id+"F0.wireOp",EDGE,"E0")])]})]});
            var Q13;
            Q13=makeQuery(id+"F3.opFillet","BLEND_EDGE",EDGE,{"blendedFrom":[makeQuery(id+"F1.opExtrude","CAP_EDGE",EDGE,{"disambiguationData":[OSD([sQuery(id+"F0.wireOp",EDGE,"E4.20.2")])],"isStart":false}),makeQuery(id+"F2.opRevolve","SWEPT_FACE",FACE,{"disambiguationData":[OSD([sQuery(id+"F0.wireOp",EDGE,"E0")])]})],"blendedInto":[makeQuery(id+"F2.opRevolve","SWEPT_FACE",FACE,{"disambiguationData":[OSD([sQuery(id+"F0.wireOp",EDGE,"E0")])]})]});
            var Q14;
            Q14=makeQuery(id+"F3.opFillet","BLEND_EDGE",EDGE,{"blendedFrom":[makeQuery(id+"F1.opExtrude","CAP_EDGE",EDGE,{"disambiguationData":[OSD([sQuery(id+"F0.wireOp",EDGE,"E4.20.0")])],"isStart":false}),makeQuery(id+"F2.opRevolve","SWEPT_FACE",FACE,{"disambiguationData":[OSD([sQuery(id+"F0.wireOp",EDGE,"E0")])]})],"blendedInto":[makeQuery(id+"F2.opRevolve","SWEPT_FACE",FACE,{"disambiguationData":[OSD([sQuery(id+"F0.wireOp",EDGE,"E0")])]})]});
            var Q15;
            Q15=makeQuery(id+"F3.opFillet","BLEND_EDGE",EDGE,{"blendedFrom":[makeQuery(id+"F1.opExtrude","CAP_EDGE",EDGE,{"disambiguationData":[OSD([sQuery(id+"F0.wireOp",EDGE,"E4.19.2")])],"isStart":false}),makeQuery(id+"F2.opRevolve","SWEPT_FACE",FACE,{"disambiguationData":[OSD([sQuery(id+"F0.wireOp",EDGE,"E0")])]})],"blendedInto":[makeQuery(id+"F2.opRevolve","SWEPT_FACE",FACE,{"disambiguationData":[OSD([sQuery(id+"F0.wireOp",EDGE,"E0")])]})]});
            var Q16;
            Q16=makeQuery(id+"F3.opFillet","BLEND_EDGE",EDGE,{"blendedFrom":[makeQuery(id+"F1.opExtrude","CAP_EDGE",EDGE,{"disambiguationData":[OSD([sQuery(id+"F0.wireOp",EDGE,"E4.2.0")])],"isStart":false}),makeQuery(id+"F2.opRevolve","SWEPT_FACE",FACE,{"disambiguationData":[OSD([sQuery(id+"F0.wireOp",EDGE,"E0")])]})],"blendedInto":[makeQuery(id+"F2.opRevolve","SWEPT_FACE",FACE,{"disambiguationData":[OSD([sQuery(id+"F0.wireOp",EDGE,"E0")])]})]});
            var Q17;
            Q17=makeQuery(id+"F3.opFillet","BLEND_EDGE",EDGE,{"blendedFrom":[makeQuery(id+"F1.opExtrude","CAP_EDGE",EDGE,{"disambiguationData":[OSD([sQuery(id+"F0.wireOp",EDGE,"E4.2.2")])],"isStart":false}),makeQuery(id+"F2.opRevolve","SWEPT_FACE",FACE,{"disambiguationData":[OSD([sQuery(id+"F0.wireOp",EDGE,"E0")])]})],"blendedInto":[makeQuery(id+"F2.opRevolve","SWEPT_FACE",FACE,{"disambiguationData":[OSD([sQuery(id+"F0.wireOp",EDGE,"E0")])]})]});
            var Q18;
            Q18=makeQuery(id+"F3.opFillet","BLEND_EDGE",EDGE,{"blendedFrom":[makeQuery(id+"F1.opExtrude","CAP_EDGE",EDGE,{"disambiguationData":[OSD([sQuery(id+"F0.wireOp",EDGE,"E4.3.0")])],"isStart":false}),makeQuery(id+"F2.opRevolve","SWEPT_FACE",FACE,{"disambiguationData":[OSD([sQuery(id+"F0.wireOp",EDGE,"E0")])]})],"blendedInto":[makeQuery(id+"F2.opRevolve","SWEPT_FACE",FACE,{"disambiguationData":[OSD([sQuery(id+"F0.wireOp",EDGE,"E0")])]})]});
            var Q19;
            Q19=makeQuery(id+"F3.opFillet","BLEND_EDGE",EDGE,{"blendedFrom":[makeQuery(id+"F1.opExtrude","CAP_EDGE",EDGE,{"disambiguationData":[OSD([sQuery(id+"F0.wireOp",EDGE,"E4.3.2")])],"isStart":false}),makeQuery(id+"F2.opRevolve","SWEPT_FACE",FACE,{"disambiguationData":[OSD([sQuery(id+"F0.wireOp",EDGE,"E0")])]})],"blendedInto":[makeQuery(id+"F2.opRevolve","SWEPT_FACE",FACE,{"disambiguationData":[OSD([sQuery(id+"F0.wireOp",EDGE,"E0")])]})]});
            var Q20;
            Q20=makeQuery(id+"F3.opFillet","BLEND_EDGE",EDGE,{"blendedFrom":[makeQuery(id+"F1.opExtrude","CAP_EDGE",EDGE,{"disambiguationData":[OSD([sQuery(id+"F0.wireOp",EDGE,"E4.4.0")])],"isStart":false}),makeQuery(id+"F2.opRevolve","SWEPT_FACE",FACE,{"disambiguationData":[OSD([sQuery(id+"F0.wireOp",EDGE,"E0")])]})],"blendedInto":[makeQuery(id+"F2.opRevolve","SWEPT_FACE",FACE,{"disambiguationData":[OSD([sQuery(id+"F0.wireOp",EDGE,"E0")])]})]});
            var Q21;
            Q21=makeQuery(id+"F3.opFillet","BLEND_EDGE",EDGE,{"blendedFrom":[makeQuery(id+"F1.opExtrude","CAP_EDGE",EDGE,{"disambiguationData":[OSD([sQuery(id+"F0.wireOp",EDGE,"E4.4.2")])],"isStart":false}),makeQuery(id+"F2.opRevolve","SWEPT_FACE",FACE,{"disambiguationData":[OSD([sQuery(id+"F0.wireOp",EDGE,"E0")])]})],"blendedInto":[makeQuery(id+"F2.opRevolve","SWEPT_FACE",FACE,{"disambiguationData":[OSD([sQuery(id+"F0.wireOp",EDGE,"E0")])]})]});
            var Q22;
            Q22=makeQuery(id+"F3.opFillet","BLEND_EDGE",EDGE,{"blendedFrom":[makeQuery(id+"F1.opExtrude","CAP_EDGE",EDGE,{"disambiguationData":[OSD([sQuery(id+"F0.wireOp",EDGE,"E4.5.0")])],"isStart":false}),makeQuery(id+"F2.opRevolve","SWEPT_FACE",FACE,{"disambiguationData":[OSD([sQuery(id+"F0.wireOp",EDGE,"E0")])]})],"blendedInto":[makeQuery(id+"F2.opRevolve","SWEPT_FACE",FACE,{"disambiguationData":[OSD([sQuery(id+"F0.wireOp",EDGE,"E0")])]})]});
            var Q23;
            Q23=makeQuery(id+"F3.opFillet","BLEND_EDGE",EDGE,{"blendedFrom":[makeQuery(id+"F1.opExtrude","CAP_EDGE",EDGE,{"disambiguationData":[OSD([sQuery(id+"F0.wireOp",EDGE,"E4.5.2")])],"isStart":false}),makeQuery(id+"F2.opRevolve","SWEPT_FACE",FACE,{"disambiguationData":[OSD([sQuery(id+"F0.wireOp",EDGE,"E0")])]})],"blendedInto":[makeQuery(id+"F2.opRevolve","SWEPT_FACE",FACE,{"disambiguationData":[OSD([sQuery(id+"F0.wireOp",EDGE,"E0")])]})]});
            var Q24;
            Q24=makeQuery(id+"F3.opFillet","BLEND_EDGE",EDGE,{"blendedFrom":[makeQuery(id+"F1.opExtrude","CAP_EDGE",EDGE,{"disambiguationData":[OSD([sQuery(id+"F0.wireOp",EDGE,"E4.6.0")])],"isStart":false}),makeQuery(id+"F2.opRevolve","SWEPT_FACE",FACE,{"disambiguationData":[OSD([sQuery(id+"F0.wireOp",EDGE,"E0")])]})],"blendedInto":[makeQuery(id+"F2.opRevolve","SWEPT_FACE",FACE,{"disambiguationData":[OSD([sQuery(id+"F0.wireOp",EDGE,"E0")])]})]});
            var Q25;
            Q25=makeQuery(id+"F3.opFillet","BLEND_EDGE",EDGE,{"blendedFrom":[makeQuery(id+"F1.opExtrude","CAP_EDGE",EDGE,{"disambiguationData":[OSD([sQuery(id+"F0.wireOp",EDGE,"E4.6.2")])],"isStart":false}),makeQuery(id+"F2.opRevolve","SWEPT_FACE",FACE,{"disambiguationData":[OSD([sQuery(id+"F0.wireOp",EDGE,"E0")])]})],"blendedInto":[makeQuery(id+"F2.opRevolve","SWEPT_FACE",FACE,{"disambiguationData":[OSD([sQuery(id+"F0.wireOp",EDGE,"E0")])]})]});
            var Q26;
            Q26=makeQuery(id+"F3.opFillet","BLEND_EDGE",EDGE,{"blendedFrom":[makeQuery(id+"F1.opExtrude","CAP_EDGE",EDGE,{"disambiguationData":[OSD([sQuery(id+"F0.wireOp",EDGE,"E4.7.0")])],"isStart":false}),makeQuery(id+"F2.opRevolve","SWEPT_FACE",FACE,{"disambiguationData":[OSD([sQuery(id+"F0.wireOp",EDGE,"E0")])]})],"blendedInto":[makeQuery(id+"F2.opRevolve","SWEPT_FACE",FACE,{"disambiguationData":[OSD([sQuery(id+"F0.wireOp",EDGE,"E0")])]})]});
            var Q27;
            Q27=makeQuery(id+"F3.opFillet","BLEND_EDGE",EDGE,{"blendedFrom":[makeQuery(id+"F1.opExtrude","CAP_EDGE",EDGE,{"disambiguationData":[OSD([sQuery(id+"F0.wireOp",EDGE,"E4.7.2")])],"isStart":false}),makeQuery(id+"F2.opRevolve","SWEPT_FACE",FACE,{"disambiguationData":[OSD([sQuery(id+"F0.wireOp",EDGE,"E0")])]})],"blendedInto":[makeQuery(id+"F2.opRevolve","SWEPT_FACE",FACE,{"disambiguationData":[OSD([sQuery(id+"F0.wireOp",EDGE,"E0")])]})]});
            var Q28;
            Q28=makeQuery(id+"F3.opFillet","BLEND_EDGE",EDGE,{"blendedFrom":[makeQuery(id+"F1.opExtrude","CAP_EDGE",EDGE,{"disambiguationData":[OSD([sQuery(id+"F0.wireOp",EDGE,"E4.8.2")])],"isStart":false}),makeQuery(id+"F2.opRevolve","SWEPT_FACE",FACE,{"disambiguationData":[OSD([sQuery(id+"F0.wireOp",EDGE,"E0")])]})],"blendedInto":[makeQuery(id+"F2.opRevolve","SWEPT_FACE",FACE,{"disambiguationData":[OSD([sQuery(id+"F0.wireOp",EDGE,"E0")])]})]});
            var Q29;
            Q29=makeQuery(id+"F3.opFillet","BLEND_EDGE",EDGE,{"blendedFrom":[makeQuery(id+"F1.opExtrude","CAP_EDGE",EDGE,{"disambiguationData":[OSD([sQuery(id+"F0.wireOp",EDGE,"E4.9.0")])],"isStart":false}),makeQuery(id+"F2.opRevolve","SWEPT_FACE",FACE,{"disambiguationData":[OSD([sQuery(id+"F0.wireOp",EDGE,"E0")])]})],"blendedInto":[makeQuery(id+"F2.opRevolve","SWEPT_FACE",FACE,{"disambiguationData":[OSD([sQuery(id+"F0.wireOp",EDGE,"E0")])]})]});
            var Q30;
            Q30=makeQuery(id+"F3.opFillet","BLEND_EDGE",EDGE,{"blendedFrom":[makeQuery(id+"F1.opExtrude","CAP_EDGE",EDGE,{"disambiguationData":[OSD([sQuery(id+"F0.wireOp",EDGE,"E4.9.2")])],"isStart":false}),makeQuery(id+"F2.opRevolve","SWEPT_FACE",FACE,{"disambiguationData":[OSD([sQuery(id+"F0.wireOp",EDGE,"E0")])]})],"blendedInto":[makeQuery(id+"F2.opRevolve","SWEPT_FACE",FACE,{"disambiguationData":[OSD([sQuery(id+"F0.wireOp",EDGE,"E0")])]})]});
            var Q31;
            Q31=makeQuery(id+"F3.opFillet","BLEND_EDGE",EDGE,{"blendedFrom":[makeQuery(id+"F1.opExtrude","CAP_EDGE",EDGE,{"disambiguationData":[OSD([sQuery(id+"F0.wireOp",EDGE,"E4.11.0")])],"isStart":false}),makeQuery(id+"F2.opRevolve","SWEPT_FACE",FACE,{"disambiguationData":[OSD([sQuery(id+"F0.wireOp",EDGE,"E0")])]})],"blendedInto":[makeQuery(id+"F2.opRevolve","SWEPT_FACE",FACE,{"disambiguationData":[OSD([sQuery(id+"F0.wireOp",EDGE,"E0")])]})]});
            var Q32;
            Q32=makeQuery(id+"F3.opFillet","BLEND_EDGE",EDGE,{"blendedFrom":[makeQuery(id+"F1.opExtrude","CAP_EDGE",EDGE,{"disambiguationData":[OSD([sQuery(id+"F0.wireOp",EDGE,"E4.10.2")])],"isStart":false}),makeQuery(id+"F2.opRevolve","SWEPT_FACE",FACE,{"disambiguationData":[OSD([sQuery(id+"F0.wireOp",EDGE,"E0")])]})],"blendedInto":[makeQuery(id+"F2.opRevolve","SWEPT_FACE",FACE,{"disambiguationData":[OSD([sQuery(id+"F0.wireOp",EDGE,"E0")])]})]});
            var Q33;
            Q33=makeQuery(id+"F3.opFillet","BLEND_EDGE",EDGE,{"blendedFrom":[makeQuery(id+"F1.opExtrude","CAP_EDGE",EDGE,{"disambiguationData":[OSD([sQuery(id+"F0.wireOp",EDGE,"E4.10.0")])],"isStart":false}),makeQuery(id+"F2.opRevolve","SWEPT_FACE",FACE,{"disambiguationData":[OSD([sQuery(id+"F0.wireOp",EDGE,"E0")])]})],"blendedInto":[makeQuery(id+"F2.opRevolve","SWEPT_FACE",FACE,{"disambiguationData":[OSD([sQuery(id+"F0.wireOp",EDGE,"E0")])]})]});
            var Q34;
            Q34=makeQuery(id+"F3.opFillet","BLEND_EDGE",EDGE,{"blendedFrom":[makeQuery(id+"F1.opExtrude","CAP_EDGE",EDGE,{"disambiguationData":[OSD([sQuery(id+"F0.wireOp",EDGE,"E4.8.0")])],"isStart":false}),makeQuery(id+"F2.opRevolve","SWEPT_FACE",FACE,{"disambiguationData":[OSD([sQuery(id+"F0.wireOp",EDGE,"E0")])]})],"blendedInto":[makeQuery(id+"F2.opRevolve","SWEPT_FACE",FACE,{"disambiguationData":[OSD([sQuery(id+"F0.wireOp",EDGE,"E0")])]})]});
            var Q35;
            Q35=makeQuery(id+"F3.opFillet","BLEND_EDGE",EDGE,{"blendedFrom":[makeQuery(id+"F1.opExtrude","CAP_EDGE",EDGE,{"disambiguationData":[OSD([sQuery(id+"F0.wireOp",EDGE,"E4.11.2")])],"isStart":false}),makeQuery(id+"F2.opRevolve","SWEPT_FACE",FACE,{"disambiguationData":[OSD([sQuery(id+"F0.wireOp",EDGE,"E0")])]})],"blendedInto":[makeQuery(id+"F2.opRevolve","SWEPT_FACE",FACE,{"disambiguationData":[OSD([sQuery(id+"F0.wireOp",EDGE,"E0")])]})]});
            var Q36;
            Q36=makeQuery(id+"F3.opFillet","BLEND_EDGE",EDGE,{"blendedFrom":[makeQuery(id+"F1.opExtrude","CAP_EDGE",EDGE,{"disambiguationData":[OSD([sQuery(id+"F0.wireOp",EDGE,"E4.12.2")])],"isStart":false}),makeQuery(id+"F2.opRevolve","SWEPT_FACE",FACE,{"disambiguationData":[OSD([sQuery(id+"F0.wireOp",EDGE,"E0")])]})],"blendedInto":[makeQuery(id+"F2.opRevolve","SWEPT_FACE",FACE,{"disambiguationData":[OSD([sQuery(id+"F0.wireOp",EDGE,"E0")])]})]});
            var Q37;
            Q37=makeQuery(id+"F3.opFillet","BLEND_EDGE",EDGE,{"blendedFrom":[makeQuery(id+"F1.opExtrude","CAP_EDGE",EDGE,{"disambiguationData":[OSD([sQuery(id+"F0.wireOp",EDGE,"E4.13.2")])],"isStart":false}),makeQuery(id+"F2.opRevolve","SWEPT_FACE",FACE,{"disambiguationData":[OSD([sQuery(id+"F0.wireOp",EDGE,"E0")])]})],"blendedInto":[makeQuery(id+"F2.opRevolve","SWEPT_FACE",FACE,{"disambiguationData":[OSD([sQuery(id+"F0.wireOp",EDGE,"E0")])]})]});
            var Q38;
            Q38=makeQuery(id+"F3.opFillet","BLEND_EDGE",EDGE,{"blendedFrom":[makeQuery(id+"F1.opExtrude","CAP_EDGE",EDGE,{"disambiguationData":[OSD([sQuery(id+"F0.wireOp",EDGE,"E4.14.0")])],"isStart":false}),makeQuery(id+"F2.opRevolve","SWEPT_FACE",FACE,{"disambiguationData":[OSD([sQuery(id+"F0.wireOp",EDGE,"E0")])]})],"blendedInto":[makeQuery(id+"F2.opRevolve","SWEPT_FACE",FACE,{"disambiguationData":[OSD([sQuery(id+"F0.wireOp",EDGE,"E0")])]})]});
            var Q39;
            Q39=makeQuery(id+"F3.opFillet","BLEND_EDGE",EDGE,{"blendedFrom":[makeQuery(id+"F1.opExtrude","CAP_EDGE",EDGE,{"disambiguationData":[OSD([sQuery(id+"F0.wireOp",EDGE,"E4.14.2")])],"isStart":false}),makeQuery(id+"F2.opRevolve","SWEPT_FACE",FACE,{"disambiguationData":[OSD([sQuery(id+"F0.wireOp",EDGE,"E0")])]})],"blendedInto":[makeQuery(id+"F2.opRevolve","SWEPT_FACE",FACE,{"disambiguationData":[OSD([sQuery(id+"F0.wireOp",EDGE,"E0")])]})]});
            var Q40;
            Q40=makeQuery(id+"F3.opFillet","BLEND_EDGE",EDGE,{"blendedFrom":[makeQuery(id+"F1.opExtrude","CAP_EDGE",EDGE,{"disambiguationData":[OSD([sQuery(id+"F0.wireOp",EDGE,"E4.15.0")])],"isStart":false}),makeQuery(id+"F2.opRevolve","SWEPT_FACE",FACE,{"disambiguationData":[OSD([sQuery(id+"F0.wireOp",EDGE,"E0")])]})],"blendedInto":[makeQuery(id+"F2.opRevolve","SWEPT_FACE",FACE,{"disambiguationData":[OSD([sQuery(id+"F0.wireOp",EDGE,"E0")])]})]});
            var Q41;
            Q41=makeQuery(id+"F3.opFillet","BLEND_EDGE",EDGE,{"blendedFrom":[makeQuery(id+"F1.opExtrude","CAP_EDGE",EDGE,{"disambiguationData":[OSD([sQuery(id+"F0.wireOp",EDGE,"E4.15.2")])],"isStart":false}),makeQuery(id+"F2.opRevolve","SWEPT_FACE",FACE,{"disambiguationData":[OSD([sQuery(id+"F0.wireOp",EDGE,"E0")])]})],"blendedInto":[makeQuery(id+"F2.opRevolve","SWEPT_FACE",FACE,{"disambiguationData":[OSD([sQuery(id+"F0.wireOp",EDGE,"E0")])]})]});
            var Q42;
            Q42=makeQuery(id+"F3.opFillet","BLEND_EDGE",EDGE,{"blendedFrom":[makeQuery(id+"F1.opExtrude","CAP_EDGE",EDGE,{"disambiguationData":[OSD([sQuery(id+"F0.wireOp",EDGE,"E4.16.0")])],"isStart":false}),makeQuery(id+"F2.opRevolve","SWEPT_FACE",FACE,{"disambiguationData":[OSD([sQuery(id+"F0.wireOp",EDGE,"E0")])]})],"blendedInto":[makeQuery(id+"F2.opRevolve","SWEPT_FACE",FACE,{"disambiguationData":[OSD([sQuery(id+"F0.wireOp",EDGE,"E0")])]})]});
            var Q43;
            Q43=makeQuery(id+"F3.opFillet","BLEND_EDGE",EDGE,{"blendedFrom":[makeQuery(id+"F1.opExtrude","CAP_EDGE",EDGE,{"disambiguationData":[OSD([sQuery(id+"F0.wireOp",EDGE,"E4.16.2")])],"isStart":false}),makeQuery(id+"F2.opRevolve","SWEPT_FACE",FACE,{"disambiguationData":[OSD([sQuery(id+"F0.wireOp",EDGE,"E0")])]})],"blendedInto":[makeQuery(id+"F2.opRevolve","SWEPT_FACE",FACE,{"disambiguationData":[OSD([sQuery(id+"F0.wireOp",EDGE,"E0")])]})]});
            var Q44;
            Q44=makeQuery(id+"F3.opFillet","BLEND_EDGE",EDGE,{"blendedFrom":[makeQuery(id+"F1.opExtrude","CAP_EDGE",EDGE,{"disambiguationData":[OSD([sQuery(id+"F0.wireOp",EDGE,"E4.17.0")])],"isStart":false}),makeQuery(id+"F2.opRevolve","SWEPT_FACE",FACE,{"disambiguationData":[OSD([sQuery(id+"F0.wireOp",EDGE,"E0")])]})],"blendedInto":[makeQuery(id+"F2.opRevolve","SWEPT_FACE",FACE,{"disambiguationData":[OSD([sQuery(id+"F0.wireOp",EDGE,"E0")])]})]});
            var Q45;
            Q45=makeQuery(id+"F3.opFillet","BLEND_EDGE",EDGE,{"blendedFrom":[makeQuery(id+"F1.opExtrude","CAP_EDGE",EDGE,{"disambiguationData":[OSD([sQuery(id+"F0.wireOp",EDGE,"E4.17.2")])],"isStart":false}),makeQuery(id+"F2.opRevolve","SWEPT_FACE",FACE,{"disambiguationData":[OSD([sQuery(id+"F0.wireOp",EDGE,"E0")])]})],"blendedInto":[makeQuery(id+"F2.opRevolve","SWEPT_FACE",FACE,{"disambiguationData":[OSD([sQuery(id+"F0.wireOp",EDGE,"E0")])]})]});
            var Q46;
            Q46=makeQuery(id+"F3.opFillet","BLEND_EDGE",EDGE,{"blendedFrom":[makeQuery(id+"F1.opExtrude","CAP_EDGE",EDGE,{"disambiguationData":[OSD([sQuery(id+"F0.wireOp",EDGE,"E4.18.0")])],"isStart":false}),makeQuery(id+"F2.opRevolve","SWEPT_FACE",FACE,{"disambiguationData":[OSD([sQuery(id+"F0.wireOp",EDGE,"E0")])]})],"blendedInto":[makeQuery(id+"F2.opRevolve","SWEPT_FACE",FACE,{"disambiguationData":[OSD([sQuery(id+"F0.wireOp",EDGE,"E0")])]})]});
            var Q47;
            Q47=makeQuery(id+"F3.opFillet","BLEND_EDGE",EDGE,{"blendedFrom":[makeQuery(id+"F1.opExtrude","CAP_EDGE",EDGE,{"disambiguationData":[OSD([sQuery(id+"F0.wireOp",EDGE,"E4.18.2")])],"isStart":false}),makeQuery(id+"F2.opRevolve","SWEPT_FACE",FACE,{"disambiguationData":[OSD([sQuery(id+"F0.wireOp",EDGE,"E0")])]})],"blendedInto":[makeQuery(id+"F2.opRevolve","SWEPT_FACE",FACE,{"disambiguationData":[OSD([sQuery(id+"F0.wireOp",EDGE,"E0")])]})]});
            var Q48;
            Q48=makeQuery(id+"F3.opFillet","BLEND_EDGE",EDGE,{"blendedFrom":[makeQuery(id+"F1.opExtrude","CAP_EDGE",EDGE,{"disambiguationData":[OSD([sQuery(id+"F0.wireOp",EDGE,"E4.19.0")])],"isStart":false}),makeQuery(id+"F2.opRevolve","SWEPT_FACE",FACE,{"disambiguationData":[OSD([sQuery(id+"F0.wireOp",EDGE,"E0")])]})],"blendedInto":[makeQuery(id+"F2.opRevolve","SWEPT_FACE",FACE,{"disambiguationData":[OSD([sQuery(id+"F0.wireOp",EDGE,"E0")])]})]});
            var Q49;
            Q49=makeQuery(id+"F3.opFillet","BLEND_EDGE",EDGE,{"blendedFrom":[makeQuery(id+"F1.opExtrude","CAP_EDGE",EDGE,{"disambiguationData":[OSD([sQuery(id+"F0.wireOp",EDGE,"E4.13.0")])],"isStart":false}),makeQuery(id+"F2.opRevolve","SWEPT_FACE",FACE,{"disambiguationData":[OSD([sQuery(id+"F0.wireOp",EDGE,"E0")])]})],"blendedInto":[makeQuery(id+"F2.opRevolve","SWEPT_FACE",FACE,{"disambiguationData":[OSD([sQuery(id+"F0.wireOp",EDGE,"E0")])]})]});
            var Q50;
            Q50=makeQuery(id+"F3.opFillet","BLEND_EDGE",EDGE,{"blendedFrom":[makeQuery(id+"F1.opExtrude","CAP_EDGE",EDGE,{"disambiguationData":[OSD([sQuery(id+"F0.wireOp",EDGE,"E4.12.0")])],"isStart":false}),makeQuery(id+"F2.opRevolve","SWEPT_FACE",FACE,{"disambiguationData":[OSD([sQuery(id+"F0.wireOp",EDGE,"E0")])]})],"blendedInto":[makeQuery(id+"F2.opRevolve","SWEPT_FACE",FACE,{"disambiguationData":[OSD([sQuery(id+"F0.wireOp",EDGE,"E0")])]})]});
            fillet(context, id + "F6", {"entities" : qUnion([Q0, Q1, Q2, Q3, Q4, Q5, Q6, Q7, Q8, Q9, Q10, Q11, Q12, Q13, Q14, Q15, Q16, Q17, Q18, Q19, Q20, Q21, Q22, Q23, Q24, Q25, Q26, Q27, Q28, Q29, Q30, Q31, Q32, Q33, Q34, Q35, Q36, Q37, Q38, Q39, Q40, Q41, Q42, Q43, Q44, Q45, Q46, Q47, Q48, Q49, Q50]), "radius" : 0.25 * mm, "tangentPropagation" : true, "allowEdgeOverflow" : false});
        }
    });
